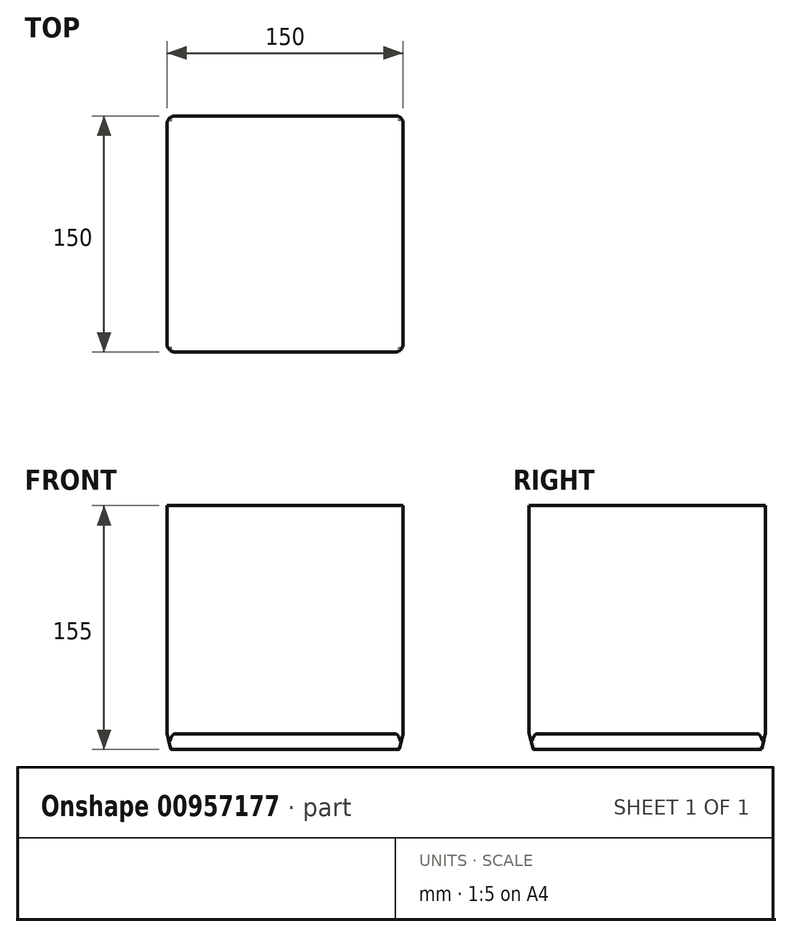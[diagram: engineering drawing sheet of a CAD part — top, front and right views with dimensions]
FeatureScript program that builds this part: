
annotation { "Feature Type Name" : "Feature", "Feature Type Description" : "" }
export const myFeature = defineFeature(function(context is Context, id is Id, definition is map)
    precondition{}
    {
        {
            var Q0;
            Q0=qCreatedBy(makeId("Top.planeOp"),FACE);
            var sketch = newSketch(context, id + "F0", { "sketchPlane" : qUnion([Q0])});
            skLineSegment(sketch, "E0.bottom", {"start": v(0, 0) * mm, "end": v(-150, 0) * mm});
            skLineSegment(sketch, "E0.top", {"start": v(0, 150) * mm, "end": v(-150, 150) * mm});
            skLineSegment(sketch, "E0.left", {"start": v(0, 0) * mm, "end": v(0, 150) * mm});
            skLineSegment(sketch, "E0.right", {"start": v(-150, 0) * mm, "end": v(-150, 150) * mm});
            skSolve(sketch);
        }
        {
            var Q0;
            Q0=makeQuery(id+"F0.imprint","IMPRINT",FACE,{"disambiguationData":[TD([[makeQuery(id+"F0.imprint","IMPRINT",EDGE,{"derivedFrom":sQuery(id+"F0.wireOp",EDGE,"E0.bottom")}),-1.0]])]});
            extrude(context, id + "F1", {"entities" : qUnion([Q0]), "depth" : 140 * mm, "offsetDistance" : 25 * mm});
        }
        {
            var Q0;
            Q0=makeQuery(id+"F1.opExtrude","CAP_FACE",FACE,{"disambiguationData":[OSD([sQuery(id+"F0.wireOp",EDGE,"E0.bottom"),sQuery(id+"F0.wireOp",EDGE,"E0.top"),sQuery(id+"F0.wireOp",EDGE,"E0.left"),sQuery(id+"F0.wireOp",EDGE,"E0.right")])],"isStart":true});
            var sketch = newSketch(context, id + "F2", { "sketchPlane" : qUnion([Q0])});
            skLineSegment(sketch, "E1.bottom", {"start": v(0, 0) * mm, "end": v(-150, 0) * mm});
            skLineSegment(sketch, "E1.top", {"start": v(0, -150) * mm, "end": v(-150, -150) * mm});
            skLineSegment(sketch, "E1.left", {"start": v(0, 0) * mm, "end": v(0, -150) * mm});
            skLineSegment(sketch, "E1.right", {"start": v(-150, 0) * mm, "end": v(-150, -150) * mm});
            skSolve(sketch);
        }
        {
            var Q0;
            Q0=makeQuery(id+"F2.imprint","IMPRINT",FACE,{"disambiguationData":[TD([[makeQuery(id+"F2.imprint","IMPRINT",EDGE,{"derivedFrom":sQuery(id+"F2.wireOp",EDGE,"E1.bottom")}),1.0]])]});
            extrude(context, id + "F3", {"entities" : qUnion([Q0]), "operationType" : NewBodyOperationType.ADD, "depth" : 15 * mm, "offsetDistance" : 25 * mm});
        }
        {
            var Q0;
            Q0=makeQuery(id+"F3.opExtrude","CAP_FACE",FACE,{"disambiguationData":[OSD([sQuery(id+"F2.wireOp",EDGE,"E1.bottom"),sQuery(id+"F2.wireOp",EDGE,"E1.top"),sQuery(id+"F2.wireOp",EDGE,"E1.left"),sQuery(id+"F2.wireOp",EDGE,"E1.right")])],"isStart":false});
            chamfer(context, id + "F4", {"entities" : qUnion([Q0]), "chamferType" : ChamferType.TWO_OFFSETS, "width1" : 2.5 * mm, "oppositeDirection" : false, "width2" : 10 * mm, "tangentPropagation" : true});
        }
        {
            var Q0;
            Q0=makeQuery(id+"F4.opChamfer","BLEND_EDGE",EDGE,{"blendedFrom":[makeQuery(id+"F3.opExtrude","CAP_EDGE",EDGE,{"disambiguationData":[OSD([sQuery(id+"F2.wireOp",EDGE,"E1.bottom")])],"isStart":false}),makeQuery(id+"F3.opExtrude","CAP_EDGE",EDGE,{"disambiguationData":[OSD([sQuery(id+"F2.wireOp",EDGE,"E1.left")])],"isStart":false})],"blendedInto":[]});
            var Q1;
            Q1=makeQuery(id+"F4.opChamfer","BLEND_EDGE",EDGE,{"blendedFrom":[makeQuery(id+"F3.opExtrude","CAP_EDGE",EDGE,{"disambiguationData":[OSD([sQuery(id+"F2.wireOp",EDGE,"E1.bottom")])],"isStart":false}),makeQuery(id+"F3.opExtrude","CAP_EDGE",EDGE,{"disambiguationData":[OSD([sQuery(id+"F2.wireOp",EDGE,"E1.right")])],"isStart":false})],"blendedInto":[]});
            var Q2;
            Q2=makeQuery(id+"F4.opChamfer","BLEND_EDGE",EDGE,{"blendedFrom":[makeQuery(id+"F3.opExtrude","CAP_EDGE",EDGE,{"disambiguationData":[OSD([sQuery(id+"F2.wireOp",EDGE,"E1.top")])],"isStart":false}),makeQuery(id+"F3.opExtrude","CAP_EDGE",EDGE,{"disambiguationData":[OSD([sQuery(id+"F2.wireOp",EDGE,"E1.right")])],"isStart":false})],"blendedInto":[]});
            var Q3;
            Q3=makeQuery(id+"F4.opChamfer","BLEND_EDGE",EDGE,{"blendedFrom":[makeQuery(id+"F3.opExtrude","CAP_EDGE",EDGE,{"disambiguationData":[OSD([sQuery(id+"F2.wireOp",EDGE,"E1.top")])],"isStart":false}),makeQuery(id+"F3.opExtrude","CAP_EDGE",EDGE,{"disambiguationData":[OSD([sQuery(id+"F2.wireOp",EDGE,"E1.left")])],"isStart":false})],"blendedInto":[]});
            var Q4;
            Q4=makeQuery(id+"F3.opExtrude","CAP_FACE",FACE,{"disambiguationData":[OSD([sQuery(id+"F2.wireOp",EDGE,"E1.bottom"),sQuery(id+"F2.wireOp",EDGE,"E1.top"),sQuery(id+"F2.wireOp",EDGE,"E1.left"),sQuery(id+"F2.wireOp",EDGE,"E1.right")])],"isStart":false});
            fillet(context, id + "F5", {"entities" : qUnion([Q0, Q1, Q2, Q3, Q4]), "radius" : 1 * mm, "tangentPropagation" : true, "allowEdgeOverflow" : false});
        }
        {
            var Q0;
            Q0=makeQuery(id+"F3.boolean.opBoolean","MERGE",EDGE,{"derivedFrom":[makeQuery(id+"F1.opExtrude","SWEPT_EDGE",EDGE,{"disambiguationData":[OSD([sQuery(id+"F0.wireOp",EDGE,"E0.bottom"),sQuery(id+"F0.wireOp",EDGE,"E0.left")])]}),makeQuery(id+"F3.opExtrude","SWEPT_EDGE",EDGE,{"disambiguationData":[OSD([sQuery(id+"F2.wireOp",EDGE,"E1.bottom"),sQuery(id+"F2.wireOp",EDGE,"E1.left")])]})]});
            var Q1;
            Q1=makeQuery(id+"F3.boolean.opBoolean","MERGE",EDGE,{"derivedFrom":[makeQuery(id+"F1.opExtrude","SWEPT_EDGE",EDGE,{"disambiguationData":[OSD([sQuery(id+"F0.wireOp",EDGE,"E0.bottom"),sQuery(id+"F0.wireOp",EDGE,"E0.right")])]}),makeQuery(id+"F3.opExtrude","SWEPT_EDGE",EDGE,{"disambiguationData":[OSD([sQuery(id+"F2.wireOp",EDGE,"E1.bottom"),sQuery(id+"F2.wireOp",EDGE,"E1.right")])]})]});
            var Q2;
            Q2=makeQuery(id+"F3.boolean.opBoolean","MERGE",EDGE,{"derivedFrom":[makeQuery(id+"F1.opExtrude","SWEPT_EDGE",EDGE,{"disambiguationData":[OSD([sQuery(id+"F0.wireOp",EDGE,"E0.top"),sQuery(id+"F0.wireOp",EDGE,"E0.right")])]}),makeQuery(id+"F3.opExtrude","SWEPT_EDGE",EDGE,{"disambiguationData":[OSD([sQuery(id+"F2.wireOp",EDGE,"E1.top"),sQuery(id+"F2.wireOp",EDGE,"E1.right")])]})]});
            var Q3;
            Q3=makeQuery(id+"F3.boolean.opBoolean","MERGE",EDGE,{"derivedFrom":[makeQuery(id+"F1.opExtrude","SWEPT_EDGE",EDGE,{"disambiguationData":[OSD([sQuery(id+"F0.wireOp",EDGE,"E0.top"),sQuery(id+"F0.wireOp",EDGE,"E0.left")])]}),makeQuery(id+"F3.opExtrude","SWEPT_EDGE",EDGE,{"disambiguationData":[OSD([sQuery(id+"F2.wireOp",EDGE,"E1.top"),sQuery(id+"F2.wireOp",EDGE,"E1.left")])]})]});
            fillet(context, id + "F6", {"entities" : qUnion([Q0, Q1, Q2, Q3]), "radius" : 5 * mm, "tangentPropagation" : true, "allowEdgeOverflow" : false});
        }
    });
